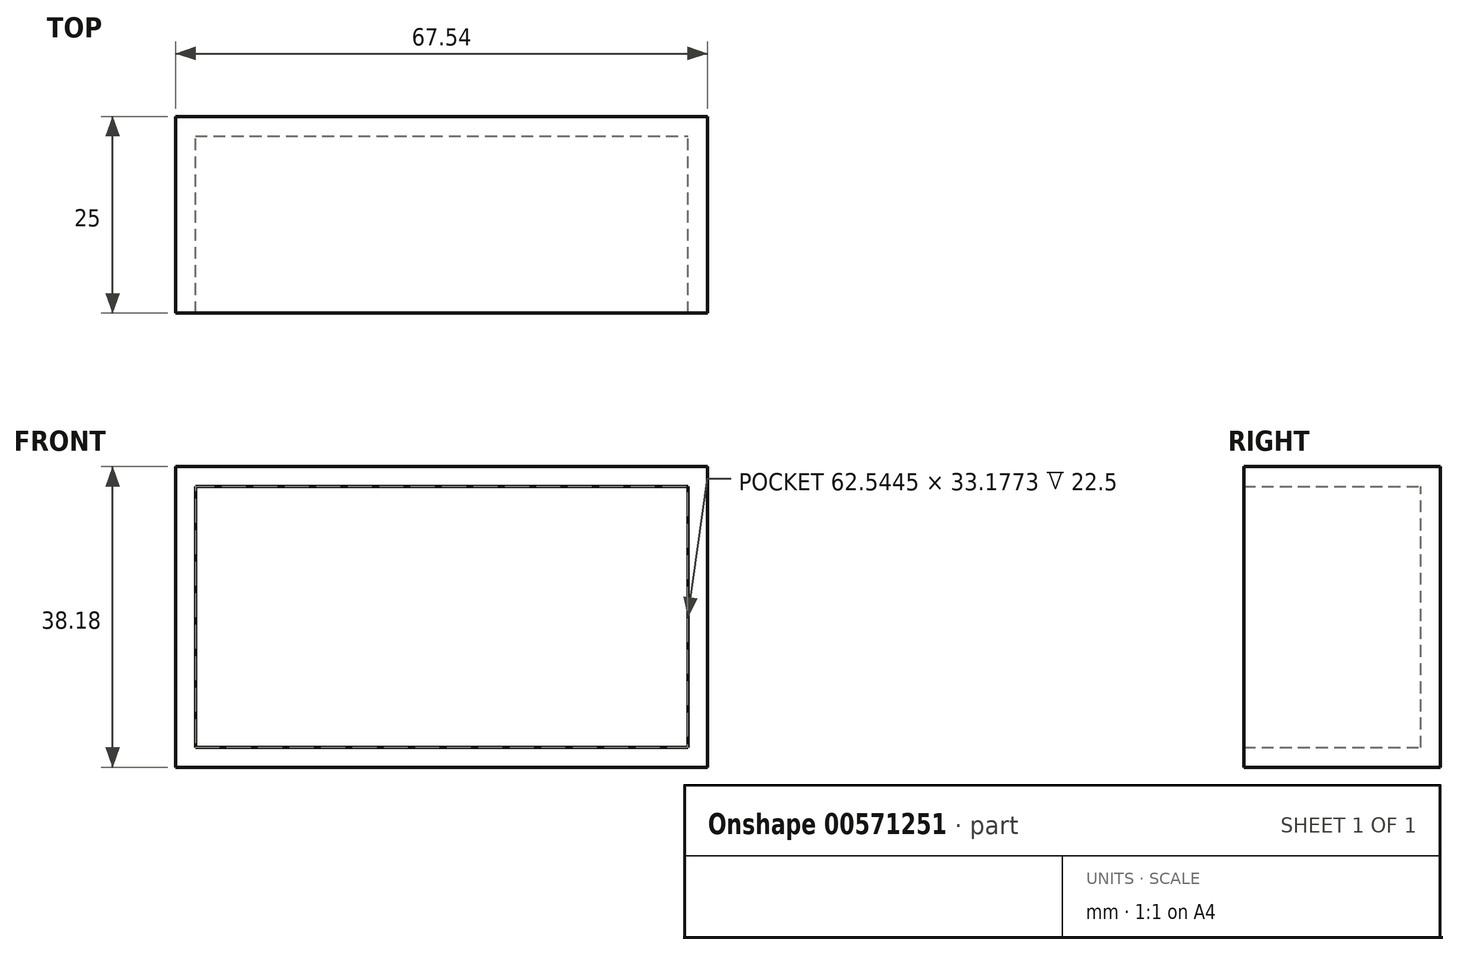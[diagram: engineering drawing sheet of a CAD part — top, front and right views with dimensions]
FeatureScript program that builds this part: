
annotation { "Feature Type Name" : "Feature", "Feature Type Description" : "" }
export const myFeature = defineFeature(function(context is Context, id is Id, definition is map)
    precondition{}
    {
        {
            var Q0;
            Q0=qCreatedBy(makeId("Front.planeOp"),FACE);
            var sketch = newSketch(context, id + "F0", { "sketchPlane" : qUnion([Q0])});
            skLineSegment(sketch, "E0.bottom", {"start": v(0, 0) * mm, "end": v(67.54, 0) * mm});
            skLineSegment(sketch, "E0.top", {"start": v(0, 38.18) * mm, "end": v(67.54, 38.18) * mm});
            skLineSegment(sketch, "E0.left", {"start": v(0, 0) * mm, "end": v(0, 38.18) * mm});
            skLineSegment(sketch, "E0.right", {"start": v(67.54, 0) * mm, "end": v(67.54, 38.18) * mm});
            skSolve(sketch);
        }
        {
            var Q0;
            Q0=makeQuery(id+"F0.imprint","IMPRINT",FACE,{"disambiguationData":[TD([[makeQuery(id+"F0.imprint","IMPRINT",EDGE,{"derivedFrom":sQuery(id+"F0.wireOp",EDGE,"E0.bottom")}),1.0]])]});
            extrude(context, id + "F1", {"entities" : qUnion([Q0]), "endBound" : BoundingType.SYMMETRIC, "depth" : 25 * mm, "offsetDistance" : 25 * mm});
        }
        {
            var Q0;
            Q0=makeQuery(id+"F1.opExtrude","CAP_FACE",FACE,{"disambiguationData":[OSD([sQuery(id+"F0.wireOp",EDGE,"E0.bottom"),sQuery(id+"F0.wireOp",EDGE,"E0.top"),sQuery(id+"F0.wireOp",EDGE,"E0.left"),sQuery(id+"F0.wireOp",EDGE,"E0.right")])],"isStart":false});
            shell(context, id + "F2", {"entities" : qUnion([Q0]), "thickness" : 2.5 * mm});
        }
    });
